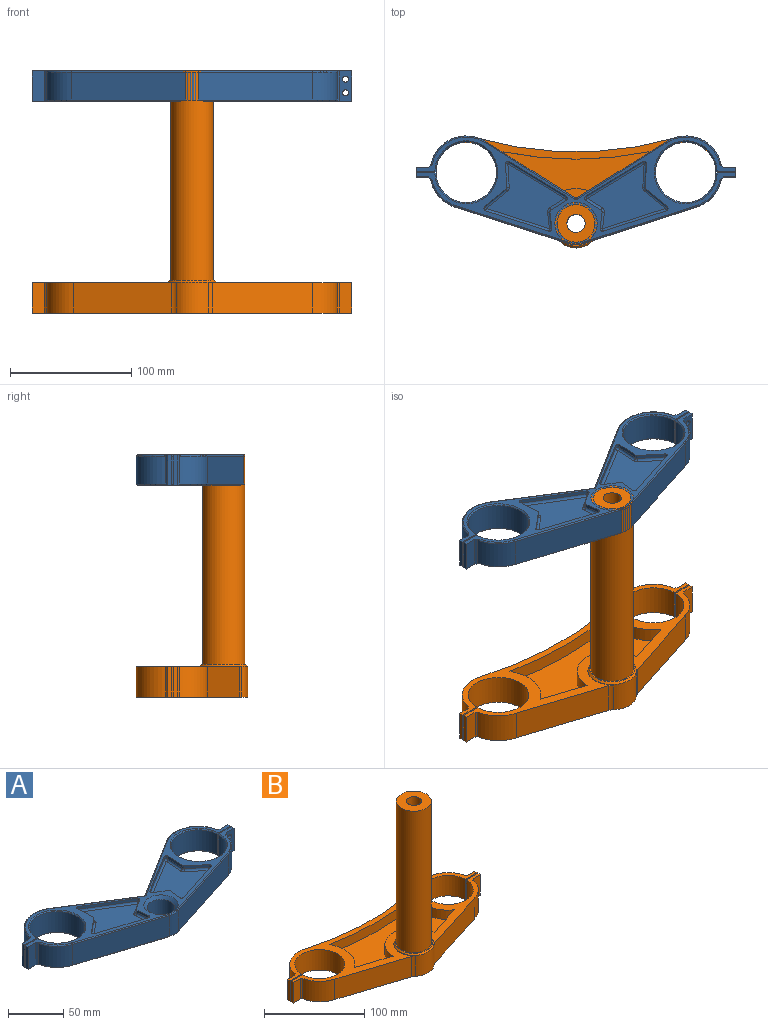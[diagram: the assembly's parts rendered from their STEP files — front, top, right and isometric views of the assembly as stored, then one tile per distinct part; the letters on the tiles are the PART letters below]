
ASSEMBLY  parts=2 mates=1
PART A: 110 faces, bbox 263.9x93.7x25 mm
  f0: plane 25x10mm, normal (0,1,0), area 210.7mm2, adj f4,f5,f6,f29,f106,f107
  f1: plane 25x10mm, normal (0,-1,0), area 210.7mm2, adj f4,f25,f26,f29,f108,f109
  f2: plane 25x16.33mm, normal (0,1,0), area 367.9mm2, adj f4,f26,f27,f29,f52,f54,f108,f109
  f3: plane 25x16.33mm, normal (0,-1,0), area 367.9mm2, adj f4,f5,f27,f29,f52,f54,f106,f107
  f4: plane 263.9x87.76mm, normal (0,0,1), area 3075.9mm2, adj f0,f1,f2,f3,f5,f6,f11,f12
  f5: plane 25x3.33mm, normal (1,0,0), area 83.3mm2, adj f0,f3,f4,f29
  f6: plane 25.03x3.1mm, normal (0.65,0.76,0), area 61.4mm2, adj f0,f4,f7,f29,f40,f47
  f7: cylinder r=30mm len=45.47mm, axis (0,0,-1), area 1344.2mm2, adj f6,f8,f40,f47
  f8: plane 74.12x46.64mm, normal (-0.53,0.85,0), area 2014.2mm2, adj f7,f37,f39,f48
  f9: plane 74.12x46.64mm, normal (0.53,0.85,0), area 2014.2mm2, adj f10,f36,f37,f51
  f10: cylinder r=30mm len=45.47mm, axis (0,0,-1), area 1344.2mm2, adj f9,f11,f35,f50
  f11: plane 25.03x3.1mm, normal (-0.65,0.76,0), area 61.4mm2, adj f4,f10,f12,f29,f35,f50
  f12: plane 25x10mm, normal (0,1,0), area 250mm2, adj f4,f11,f13,f29
  f13: plane 25x3.33mm, normal (-1,0,0), area 83.3mm2, adj f4,f12,f14,f29
  f14: plane 25x16.33mm, normal (0,-1,0), area 407.1mm2, adj f4,f13,f15,f29,f53,f55
  f15: cylinder r=25mm len=50mm, axis (0,0,-1), area 3585.2mm2, adj f14,f16,f53,f55
  f16: plane 25x16.33mm, normal (0,1,0), area 407.1mm2, adj f4,f15,f17,f29,f53,f55
  f17: plane 25x3.33mm, normal (-1,0,0), area 83.3mm2, adj f4,f16,f18,f29
  f18: plane 25x10mm, normal (0,-1,0), area 250mm2, adj f4,f17,f19,f29
  f19: plane 25.03x3.1mm, normal (-0.65,-0.76,0), area 61.4mm2, adj f4,f18,f20,f29,f30,f42
  f20: cylinder r=30mm len=23.06mm, axis (0,0,-1), area 742mm2, adj f19,f21,f30,f42
  f21: plane 94.46x30.36mm, normal (-0.31,-0.95,0), area 2282mm2, adj f20,f22,f31,f43
  f22: cylinder r=17.5mm len=23mm, axis (0,0,-1), area 250.4mm2, adj f21,f23,f32,f44
  f23: plane 94.46x30.36mm, normal (0.31,-0.95,0), area 2282mm2, adj f22,f24,f33,f45
  f24: cylinder r=30mm len=23.06mm, axis (0,0,-1), area 742mm2, adj f23,f25,f34,f46
  f25: plane 25.03x3.1mm, normal (0.65,-0.76,0), area 61.4mm2, adj f1,f4,f24,f29,f34,f46
  f26: plane 25x3.33mm, normal (1,0,0), area 83.3mm2, adj f1,f2,f4,f29
  f27: cylinder r=25mm len=50mm, axis (0,0,-1), area 3585.2mm2, adj f2,f3,f52,f54
  f28: cylinder r=12.5mm len=25mm, axis (0,0,-1), area 1727.9mm2, adj f29,f41
  f29: plane 263.9x87.76mm, normal (0,0,-1), area 7228.5mm2, adj f0,f1,f2,f3,f5,f6,f11,f12
  f30: torus R=29mm, axis (0,0,1), area 49.3mm2, adj f4,f19,f20,f31
  f31: cylinder r=1mm len=94.76mm, axis (-0.95,0.31,0), area 155.8mm2, adj f4,f21,f30,f32
  f32: torus R=16.5mm, axis (0,0,1), area 16.7mm2, adj f4,f22,f31,f33
  f33: cylinder r=1mm len=94.76mm, axis (-0.95,-0.31,0), area 155.8mm2, adj f4,f23,f32,f34
  f34: torus R=29mm, axis (0,0,1), area 49.3mm2, adj f4,f24,f25,f33
  f35: torus R=29mm, axis (0,0,1), area 90mm2, adj f4,f10,f11,f36
  f36: cylinder r=1mm len=74.65mm, axis (0.85,-0.53,0), area 137.6mm2, adj f4,f9,f35,f38
  f37: cylinder r=1mm len=23mm, axis (0,0,-1), area 25.8mm2, adj f8,f9,f38,f49
  f38: torus R=2mm, axis (0,0,1), area 2.4mm2, adj f4,f36,f37,f39
  f39: cylinder r=1mm len=74.65mm, axis (0.85,0.53,0), area 137.6mm2, adj f4,f8,f38,f40
  f40: torus R=29mm, axis (0,0,1), area 90mm2, adj f4,f6,f7,f39
  f41: cone r=12.5mm half-angle=45deg, axis (0,0,1), area 373.2mm2, adj f4,f28
  f42: cone r=29mm half-angle=45deg, axis (0,0,1), area 43.9mm2, adj f19,f20,f29,f43
  f43: plane 94.76x31.31mm, normal (-0.22,-0.67,-0.71), area 140.3mm2, adj f21,f29,f42,f44
  f44: cone r=17.5mm half-angle=45deg, axis (0,0,1), area 15mm2, adj f22,f29,f43,f45
  f45: plane 94.76x31.31mm, normal (0.22,-0.67,-0.71), area 140.3mm2, adj f23,f29,f44,f46
  f46: cone r=30mm half-angle=45deg, axis (0,0,1), area 43.9mm2, adj f24,f25,f29,f45
  f47: cone r=30mm half-angle=45deg, axis (0,0,1), area 80.4mm2, adj f6,f7,f29,f48
  f48: plane 74.65x47.49mm, normal (-0.38,0.6,-0.71), area 123.8mm2, adj f8,f29,f47,f49
  f49: cone r=2mm half-angle=45deg, axis (0,0,-1), area 2.4mm2, adj f29,f37,f48,f51
  f50: cone r=29mm half-angle=45deg, axis (0,0,1), area 80.4mm2, adj f10,f11,f29,f51
  f51: plane 74.65x47.49mm, normal (0.38,0.6,-0.71), area 123.8mm2, adj f9,f29,f49,f50
  f52: cone r=26mm half-angle=45deg, axis (0,0,-1), area 224.9mm2, adj f2,f3,f27,f29
  f53: cone r=25mm half-angle=45deg, axis (0,0,-1), area 224.9mm2, adj f14,f15,f16,f29
  f54: cone r=25mm half-angle=45deg, axis (0,0,1), area 224.9mm2, adj f2,f3,f4,f27
  f55: cone r=26mm half-angle=45deg, axis (0,0,1), area 224.9mm2, adj f4,f14,f15,f16
  f56: plane 13.39x3mm, normal (-0.99,-0.12,0), area 40.4mm2, adj f4,f57,f67,f89
  f57: cylinder r=2mm len=3mm, axis (0,0,1), area 6.7mm2, adj f4,f56,f58,f87
  f58: plane 12.54x7.93mm, normal (-0.53,0.85,0), area 44.5mm2, adj f4,f57,f59,f85
  f59: cylinder r=2mm len=3.4mm, axis (0,0,1), area 12.2mm2, adj f4,f58,f60,f83
  f60: plane 47.16x28.67mm, normal (-0.52,-0.85,0), area 165.6mm2, adj f4,f59,f61,f82
  f61: cylinder r=2mm len=3.04mm, axis (0,0,1), area 13mm2, adj f4,f60,f62,f84
  f62: plane 19.45x3mm, normal (1,0.06,0), area 58.4mm2, adj f4,f61,f63,f86
  f63: cylinder r=2mm len=3mm, axis (0,0,1), area 5.6mm2, adj f4,f62,f64,f88
  f64: plane 17.4x14.32mm, normal (0.64,-0.77,0), area 67.6mm2, adj f4,f63,f65,f90
  f65: cylinder r=2mm len=3.45mm, axis (0,0,1), area 12.9mm2, adj f4,f64,f66,f92
  f66: plane 52.09x16.74mm, normal (0.31,0.95,0), area 164.2mm2, adj f4,f65,f67,f93
  f67: cylinder r=2mm len=3mm, axis (0,0,1), area 12mm2, adj f4,f56,f66,f91
  f68: plane 64.91x53.83mm, normal (0,0,1), area 1554.8mm2, adj f82,f85,f86,f87,f88,f89,f90,f93
  f69: cylinder r=2mm len=3.45mm, axis (0,0,1), area 12.9mm2, adj f4,f70,f80,f104
  f70: plane 17.4x14.32mm, normal (-0.64,-0.77,0), area 67.6mm2, adj f4,f69,f71,f102
  f71: cylinder r=2mm len=3mm, axis (0,0,1), area 5.6mm2, adj f4,f70,f72,f100
  f72: plane 19.45x3mm, normal (-1,0.06,0), area 58.4mm2, adj f4,f71,f73,f98
  f73: cylinder r=2mm len=3.04mm, axis (0,0,1), area 13mm2, adj f4,f72,f74,f96
  f74: plane 47.16x28.67mm, normal (0.52,-0.85,0), area 165.6mm2, adj f4,f73,f75,f94
  f75: cylinder r=2mm len=3.4mm, axis (0,0,1), area 12.2mm2, adj f4,f74,f76,f95
  f76: plane 12.54x7.93mm, normal (0.53,0.85,0), area 44.5mm2, adj f4,f75,f77,f97
  f77: cylinder r=2mm len=3mm, axis (0,0,1), area 6.7mm2, adj f4,f76,f78,f99
  f78: plane 13.39x3mm, normal (0.99,-0.12,0), area 40.4mm2, adj f4,f77,f79,f101
  f79: cylinder r=2mm len=3mm, axis (0,0,1), area 12mm2, adj f4,f78,f80,f103
  f80: plane 52.09x16.74mm, normal (-0.31,0.95,0), area 164.2mm2, adj f4,f69,f79,f105
  f81: plane 64.91x53.83mm, normal (0,0,1), area 1554.8mm2, adj f94,f97,f98,f99,f100,f101,f102,f105
  f82: cylinder r=2mm len=48.2mm, axis (-0.85,0.52,0), area 173.4mm2, adj f60,f68,f83,f84
  f83: sphere r=2mm, area 8.1mm2, adj f59,f82,f85
  f84: sphere r=2mm, area 8.7mm2, adj f61,f82,f86
  f85: cylinder r=2mm len=13.61mm, axis (0.85,0.53,0), area 46.6mm2, adj f58,f68,f83,f87
  f86: cylinder r=2mm len=19.56mm, axis (0.06,-1,0), area 61.2mm2, adj f62,f68,f84,f88
  f87: torus R=4mm, axis (0,0,1), area 9.6mm2, adj f57,f68,f85,f89
  f88: torus R=4mm, axis (0,0,1), area 8mm2, adj f63,f68,f86,f90
  f89: cylinder r=2mm len=13.62mm, axis (-0.12,0.99,0), area 42.3mm2, adj f56,f68,f87,f91
  f90: cylinder r=2mm len=18.68mm, axis (-0.77,-0.64,0), area 70.8mm2, adj f64,f68,f88,f92
  f91: sphere r=2mm, area 8mm2, adj f67,f89,f93
  f92: sphere r=2mm, area 8.6mm2, adj f65,f90,f93
  f93: cylinder r=2mm len=52.7mm, axis (0.95,-0.31,0), area 171.9mm2, adj f66,f68,f91,f92
  f94: cylinder r=2mm len=48.2mm, axis (-0.85,-0.52,0), area 173.4mm2, adj f74,f81,f95,f96
  f95: sphere r=2mm, area 8.1mm2, adj f75,f94,f97
  f96: sphere r=2mm, area 8.7mm2, adj f73,f94,f98
  f97: cylinder r=2mm len=13.61mm, axis (0.85,-0.53,0), area 46.6mm2, adj f76,f81,f95,f99
  f98: cylinder r=2mm len=19.56mm, axis (0.06,1,0), area 61.2mm2, adj f72,f81,f96,f100
  f99: torus R=4mm, axis (0,0,1), area 9.6mm2, adj f77,f81,f97,f101
  f100: torus R=4mm, axis (0,0,1), area 8mm2, adj f71,f81,f98,f102
  f101: cylinder r=2mm len=13.62mm, axis (-0.12,-0.99,0), area 42.3mm2, adj f78,f81,f99,f103
  f102: cylinder r=2mm len=18.68mm, axis (-0.77,0.64,0), area 70.8mm2, adj f70,f81,f100,f104
  f103: sphere r=2mm, area 8mm2, adj f79,f101,f105
  f104: sphere r=2mm, area 8.6mm2, adj f69,f102,f105
  f105: cylinder r=2mm len=52.7mm, axis (0.95,0.31,0), area 171.9mm2, adj f80,f81,f103,f104
  f106: cylinder r=2.5mm len=5mm, axis (0,1,0), area 52.3mm2, adj f0,f3
  f107: cylinder r=2.5mm len=5mm, axis (0,1,0), area 52.3mm2, adj f0,f3
  f108: cylinder r=2.5mm len=5mm, axis (0,1,0), area 52.3mm2, adj f1,f2
  f109: cylinder r=2.5mm len=5mm, axis (0,1,0), area 52.3mm2, adj f1,f2
PART B: 42 faces, bbox 263.9x92.3x200 mm
  f0: plane 263.91x87.27mm, normal (0,0,1), area 5211.2mm2, adj f1,f7,f8,f9,f10,f11,f12,f13
  f1: cylinder r=20mm len=40mm, axis (0,0,-1), area 785mm2, adj f0,f3,f32,f33,f34
  f2: plane 37x37mm, normal (0,0,1), area 113.1mm2, adj f4,f32
  f3: plane 263.91x92.26mm, normal (0,0,-1), area 11233.7mm2, adj f1,f5,f7,f8,f9,f10,f11,f12
  f4: cylinder r=17.5mm len=173mm, axis (0,0,-1), area 19022.3mm2, adj f2,f6
  f5: cylinder r=7.5mm len=200mm, axis (0,0,-1), area 9424.8mm2, adj f3,f6
  f6: plane 35x35mm, normal (0,0,1), area 785.4mm2, adj f4,f5
  f7: cylinder r=295.3mm len=164.56mm, axis (0,0,-1), area 4169.1mm2, adj f0,f3,f8,f31
  f8: cylinder r=30mm len=37.85mm, axis (0,0,-1), area 1251.8mm2, adj f0,f3,f7,f9
  f9: plane 25x1.83mm, normal (-0.65,0.76,0), area 60.2mm2, adj f0,f3,f8,f10
  f10: plane 25x10mm, normal (0,1,0), area 250mm2, adj f0,f3,f9,f11
  f11: plane 25x3.33mm, normal (-1,0,0), area 83.3mm2, adj f0,f3,f10,f12
  f12: plane 25x16.33mm, normal (0,-1,0), area 408.1mm2, adj f0,f3,f11,f13
  f13: cylinder r=25mm len=50mm, axis (0,0,-1), area 3897mm2, adj f0,f3,f12,f14
  f14: plane 25x16.33mm, normal (0,1,0), area 408.1mm2, adj f0,f3,f13,f15
  f15: plane 25x3.33mm, normal (-1,0,0), area 83.3mm2, adj f0,f3,f14,f16
  f16: plane 25x10mm, normal (0,-1,0), area 250mm2, adj f0,f3,f15,f17
  f17: plane 25x1.83mm, normal (-0.65,-0.76,0), area 60.2mm2, adj f0,f3,f16,f18
  f18: cylinder r=30mm len=25mm, axis (0,0,-1), area 847.5mm2, adj f0,f3,f17,f19
  f19: plane 81.47x26.19mm, normal (-0.31,-0.95,0), area 2139.3mm2, adj f0,f3,f18,f33
  f20: plane 83.04x26.69mm, normal (0.31,-0.95,0), area 2180.7mm2, adj f0,f3,f21,f34
  f21: cylinder r=30mm len=25mm, axis (0,0,-1), area 806.5mm2, adj f0,f3,f20,f22
  f22: plane 25x1.83mm, normal (0.65,-0.76,0), area 60.2mm2, adj f0,f3,f21,f23
  f23: plane 25x10mm, normal (0,-1,0), area 250mm2, adj f0,f3,f22,f24
  f24: plane 25x3.33mm, normal (1,0,0), area 83.3mm2, adj f0,f3,f23,f25
  f25: plane 25x16.33mm, normal (0,1,0), area 408.1mm2, adj f0,f3,f24,f26
  f26: cylinder r=25mm len=50mm, axis (0,0,-1), area 3897mm2, adj f0,f3,f25,f27
  f27: plane 25x16.33mm, normal (0,-1,0), area 408.1mm2, adj f0,f3,f26,f28
  f28: plane 25x3.33mm, normal (1,0,0), area 83.3mm2, adj f0,f3,f27,f29
  f29: plane 25x10mm, normal (0,1,0), area 250mm2, adj f0,f3,f28,f30
  f30: plane 25x1.83mm, normal (0.65,0.76,0), area 60.2mm2, adj f0,f3,f29,f31
  f31: cylinder r=30mm len=37.86mm, axis (0,0,-1), area 1251.7mm2, adj f0,f3,f7,f30
  f32: cone r=18.5mm half-angle=45deg, axis (0,0,-1), area 256.6mm2, adj f1,f2
  f33: cylinder r=10mm len=25mm, axis (0,0,-1), area 102.8mm2, adj f0,f1,f3,f19
  f34: cylinder r=10mm len=25mm, axis (0,0,-1), area 102.8mm2, adj f0,f1,f3,f20
  f35: plane 41.57x13.36mm, normal (-0.31,0.95,0), area 497.8mm2, adj f0,f36,f40,f41
  f36: cylinder r=35mm len=45.86mm, axis (0,0,1), area 587.9mm2, adj f0,f35,f37,f41
  f37: cylinder r=301.3mm len=120.29mm, axis (0,0,1), area 1380.6mm2, adj f0,f36,f38,f41
  f38: cylinder r=35mm len=45.86mm, axis (0,0,1), area 587.9mm2, adj f0,f37,f39,f41
  f39: plane 41.57x13.36mm, normal (0.31,0.95,0), area 497.8mm2, adj f0,f38,f40,f41
  f40: cylinder r=29mm len=58mm, axis (0,0,1), area 1034mm2, adj f0,f35,f39,f41
  f41: plane 141.14x59.25mm, normal (0,0,1), area 4942.6mm2, adj f35,f36,f37,f38,f39,f40
PLACE A t=(-41.49,-38.33,6.99)mm fixed
PLACE B t=(-36.29,-5.49,-18.01)mm
MATE fastened B.f1 <-> A.f22  axis (0,0,1) through (-41.49,-38.33,31.99)mm
